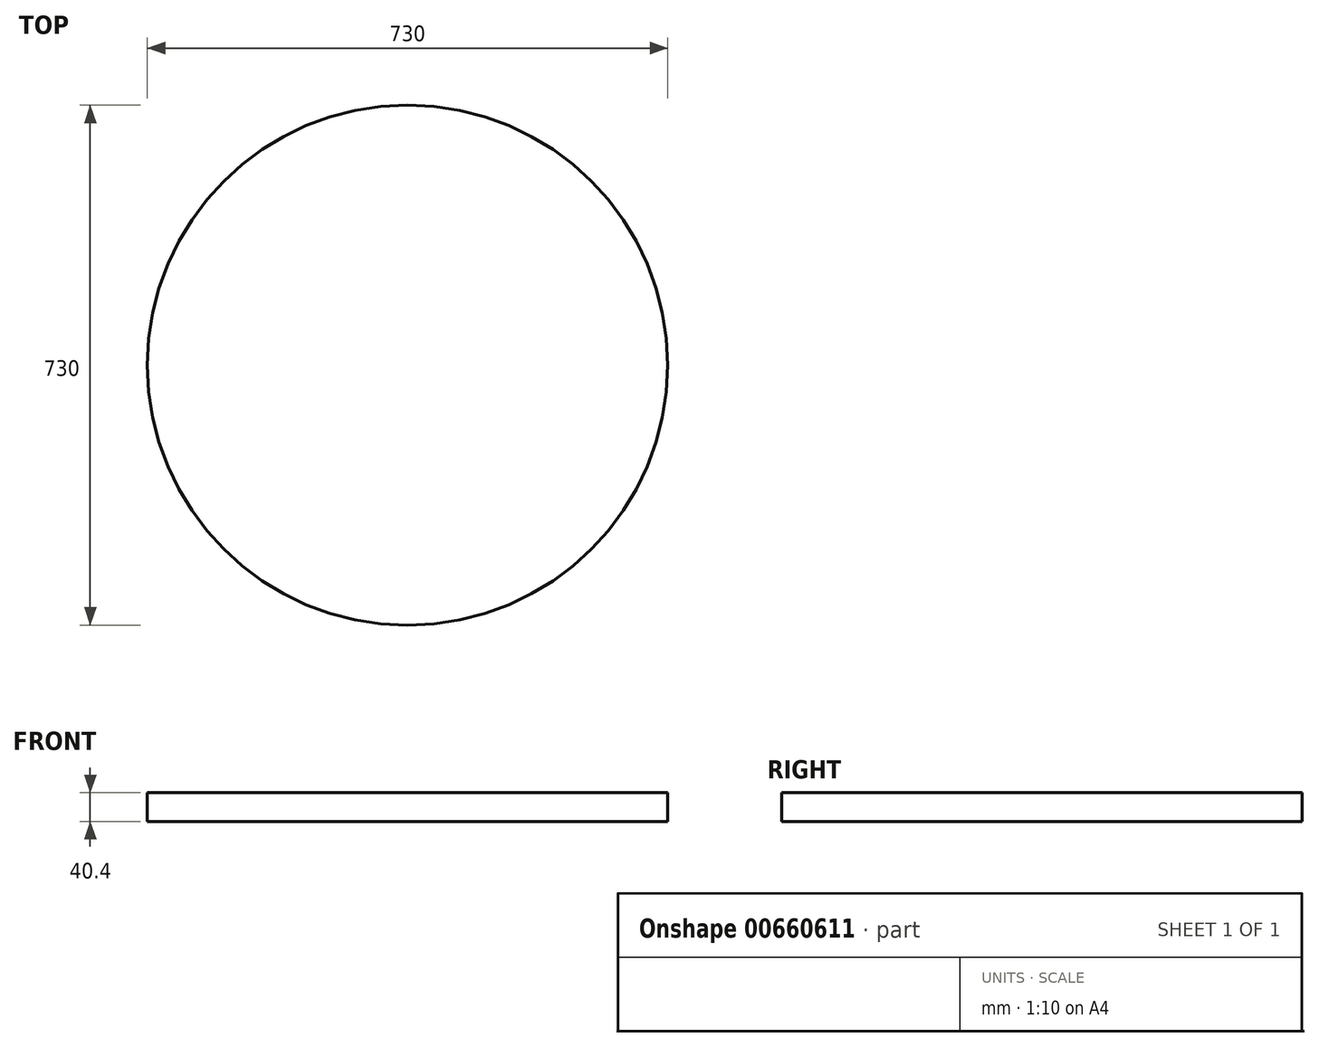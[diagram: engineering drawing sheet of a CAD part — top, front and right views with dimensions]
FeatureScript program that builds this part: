
annotation { "Feature Type Name" : "Feature", "Feature Type Description" : "" }
export const myFeature = defineFeature(function(context is Context, id is Id, definition is map)
    precondition{}
    {
        {
            var Q0;
            Q0=qCreatedBy(makeId("Front.planeOp"),FACE);
            var sketch = newSketch(context, id + "F0", { "sketchPlane" : qUnion([Q0])});
            skLineSegment(sketch, "E0", {"start": v(365, 40.4) * mm, "end": v(365, 0) * mm});
            skLineSegment(sketch, "E1", {"start": v(0, 0) * mm, "end": v(365, 0) * mm});
            skLineSegment(sketch, "E2", {"start": v(365, 40.4) * mm, "end": v(0, 40.4) * mm});
            skLineSegment(sketch, "E3", {"start": v(0, 40.4) * mm, "end": v(0, 0) * mm});
            skSolve(sketch);
        }
        {
            var Q0;
            Q0=qCreatedBy(makeId("Front.planeOp"),FACE);
            var sketch = newSketch(context, id + "F1", { "sketchPlane" : qUnion([Q0])});
            skLineSegment(sketch, "E4", {"start": v(0, 70.74) * mm, "end": v(0, -38.09) * mm});
            skSolve(sketch);
        }
        {
            var Q0;
            Q0=qSketchRegion(id+"F0",true);
            var Q1;
            Q1=sQuery(id+"F1.wireOp",EDGE,"E4");
            revolve(context, id + "F2", {"entities" : qUnion([Q0]), "axis" : qUnion([Q1]), "revolveType" : RevolveType.FULL});
        }
    });
